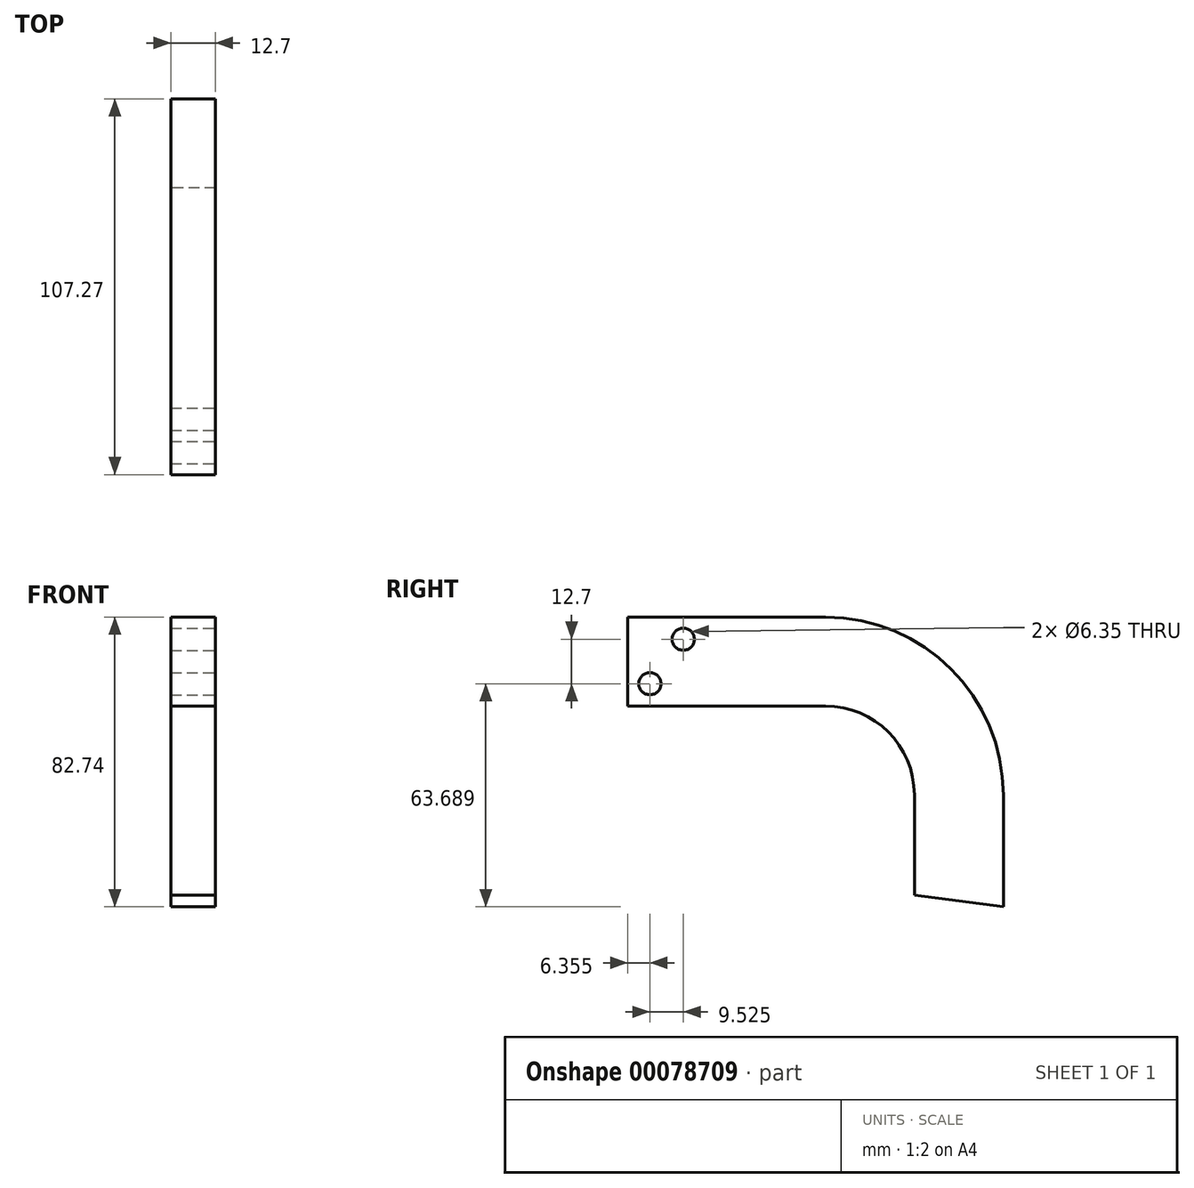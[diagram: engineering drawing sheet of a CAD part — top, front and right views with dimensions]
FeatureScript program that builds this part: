
annotation { "Feature Type Name" : "Feature", "Feature Type Description" : "" }
export const myFeature = defineFeature(function(context is Context, id is Id, definition is map)
    precondition{}
    {
        {
            var Q0;
            Q0=qCreatedBy(makeId("Right.planeOp"),FACE);
            var sketch = newSketch(context, id + "F0", { "sketchPlane" : qUnion([Q0])});
            skLineSegment(sketch, "E0.top", {"start": v(-57.14, 11.66) * mm, "end": v(-0.67, 11.66) * mm});
            skLineSegment(sketch, "E0.left", {"start": v(-57.14, 37.06) * mm, "end": v(-57.14, 11.66) * mm});
            skLineSegment(sketch, "E1", {"start": v(24.73, -13.74) * mm, "end": v(24.73, -42.32) * mm});
            skLineSegment(sketch, "E2", {"start": v(50.13, -45.68) * mm, "end": v(24.73, -42.32) * mm});
            skPoint(sketch, "E3.visualSharp", {"position": v(24.73, 11.66) * mm});
            skArc(sketch, "E3.filletArc", {"start": v(24.73, -13.74) * mm, "mid": v(17.29, 4.22) * mm, "end": v(-0.67, 11.66) * mm});
            skLineSegment(sketch, "E4.0", {"start": v(50.13, -13.74) * mm, "end": v(50.13, -45.68) * mm});
            skArc(sketch, "E4.1", {"start": v(50.13, -13.74) * mm, "mid": v(35.25, 22.18) * mm, "end": v(-0.67, 37.06) * mm});
            skLineSegment(sketch, "E4.2", {"start": v(-76.19, 37.06) * mm, "end": v(-0.67, 37.06) * mm});
            skPoint(sketch, "E5.orphan", {"position": v(69.18, -48.2) * mm});
            skSolve(sketch);
        }
        {
            var Q0;
            Q0 = qSketchRegion(id + "F0", true);
            extrude(context, id + "F1", {"entities" : qUnion([Q0]), "depth" : 12.7 * mm});
        }
        {
            var Q0;
            Q0=makeQuery(id+"F1.opExtrude","CAP_FACE",FACE,{"disambiguationData":[OSD([sQuery(id+"F0.wireOp",EDGE,"E0.top"),sQuery(id+"F0.wireOp",EDGE,"E0.left"),sQuery(id+"F0.wireOp",EDGE,"E1"),sQuery(id+"F0.wireOp",EDGE,"E2"),sQuery(id+"F0.wireOp",EDGE,"E3.filletArc"),sQuery(id+"F0.wireOp",EDGE,"E4.0"),sQuery(id+"F0.wireOp",EDGE,"E4.1"),sQuery(id+"F0.wireOp",EDGE,"E4.2")])],"isStart":false});
            var sketch = newSketch(context, id + "F2", { "sketchPlane" : qUnion([Q0])});
            skCircle(sketch, "E6", {"center": v(-50.79, 18) * mm, "radius": 3.18 * mm});
            skCircle(sketch, "E7", {"center": v(-41.26, 30.7) * mm, "radius": 3.18 * mm});
            skSolve(sketch);
        }
        {
            var Q0;
            Q0=sQuery(id+"F2.wireOp",VERTEX,"E6.center");
            var Q1;
            Q1=sQuery(id+"F2.wireOp",VERTEX,"E7.center");
            var Q2;
            Q2=makeQuery(id+"F1.opExtrude","SWEPT_BODY",BODY,{"disambiguationData":[OSD([sQuery(id+"F0.wireOp",EDGE,"E0.top"),sQuery(id+"F0.wireOp",EDGE,"E0.left"),sQuery(id+"F0.wireOp",EDGE,"E1"),sQuery(id+"F0.wireOp",EDGE,"E2"),sQuery(id+"F0.wireOp",EDGE,"E3.filletArc"),sQuery(id+"F0.wireOp",EDGE,"E4.0"),sQuery(id+"F0.wireOp",EDGE,"E4.1"),sQuery(id+"F0.wireOp",EDGE,"E4.2")])]});
            hole(context, id + "F3", {"style" : HoleStyle.SIMPLE, "endStyle" : HoleEndStyle.THROUGH, "holeDiameter" : 6.35 * mm, "locations" : qUnion([Q0, Q1]), "scope" : qUnion([Q2]), "isTappedThrough" : true});
        }
    });
